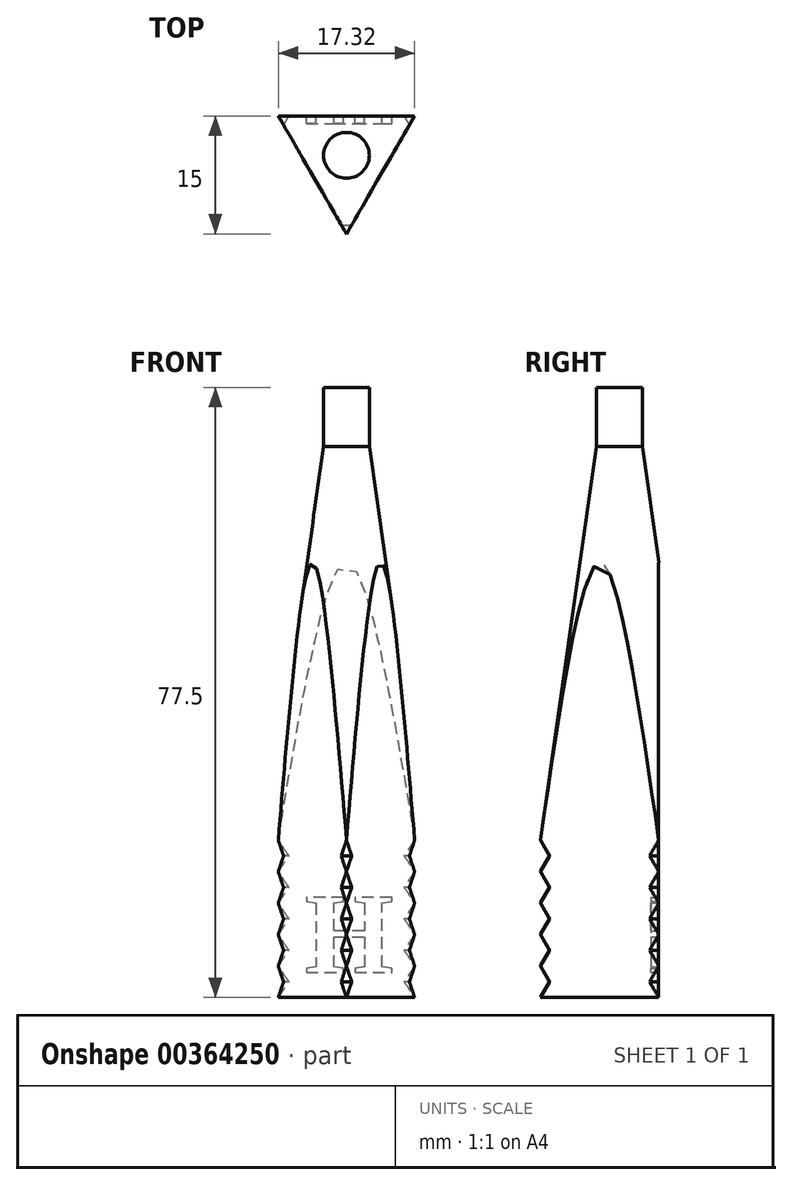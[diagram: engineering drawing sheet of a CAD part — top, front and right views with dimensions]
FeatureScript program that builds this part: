
annotation { "Feature Type Name" : "Feature", "Feature Type Description" : "" }
export const myFeature = defineFeature(function(context is Context, id is Id, definition is map)
    precondition{}
    {
        {
            var Q0;
            Q0=qCreatedBy(makeId("Top.planeOp"),FACE);
            var sketch = newSketch(context, id + "F0", { "sketchPlane" : qUnion([Q0])});
            skCircle(sketch, "E0", {"center": v(0, 0) * mm, "radius": 10 * mm, "construction": true});
            skLineSegment(sketch, "E1", {"start": v(0, -10) * mm, "end": v(-8.66, 5) * mm});
            skLineSegment(sketch, "E2", {"start": v(-8.66, 5) * mm, "end": v(8.66, 5) * mm});
            skLineSegment(sketch, "E3", {"start": v(8.66, 5) * mm, "end": v(0, -10) * mm});
            skSolve(sketch);
        }
        {
            var Q0;
            Q0=makeQuery(id+"F0.imprint","IMPRINT",FACE,{"disambiguationData":[TD([[makeQuery(id+"F0.imprint","IMPRINT",EDGE,{"derivedFrom":sQuery(id+"F0.wireOp",EDGE,"E1")}),-1.0]])]});
            extrude(context, id + "F1", {"entities" : qUnion([Q0]), "offsetDistance" : 25 * mm, "depth" : 20 * mm});
        }
        {
            var Q0;
            Q0=qCreatedBy(makeId("Right.planeOp"),FACE);
            var sketch = newSketch(context, id + "F2", { "sketchPlane" : qUnion([Q0])});
            skLineSegment(sketch, "E4", {"start": v(-2.91, 70) * mm, "end": v(-10, 20) * mm});
            skLineSegment(sketch, "E5", {"start": v(-10, 20) * mm, "end": v(0, 20) * mm});
            skLineSegment(sketch, "E6", {"start": v(0, 20) * mm, "end": v(0, 70) * mm});
            skLineSegment(sketch, "E7", {"start": v(-2.91, 70) * mm, "end": v(0, 70) * mm, "construction": true});
            skLineSegment(sketch, "E8", {"start": v(-2.91, 70) * mm, "end": v(-2.91, 76.5) * mm});
            skLineSegment(sketch, "E9", {"start": v(-2.91, 76.5) * mm, "end": v(0, 76.5) * mm});
            skLineSegment(sketch, "E10", {"start": v(0, 76.5) * mm, "end": v(0, 70) * mm});
            skSolve(sketch);
        }
        {
            var Q0;
            Q0=makeQuery(id+"F2.imprint","IMPRINT",FACE,{"disambiguationData":[TD([[makeQuery(id+"F2.imprint","IMPRINT",EDGE,{"derivedFrom":sQuery(id+"F2.wireOp",EDGE,"E4")}),1.0]])]});
            var Q1;
            Q1=sQuery(id+"F2.wireOp",EDGE,"E6");
            revolve(context, id + "F3", {"operationType" : NewBodyOperationType.ADD, "entities" : qUnion([Q0]), "axis" : qUnion([Q1]), "revolveType" : RevolveType.FULL});
        }
        {
            var Q0;
            Q0=qCreatedBy(makeId("Front.planeOp"),FACE);
            var sketch = newSketch(context, id + "F4", { "sketchPlane" : qUnion([Q0])});
            skLineSegment(sketch, "E11", {"start": v(-10, 20) * mm, "end": v(-10, 0) * mm});
            skLineSegment(sketch, "E12", {"start": v(-10, 20) * mm, "end": v(-8.86, 18) * mm});
            skLineSegment(sketch, "E13", {"start": v(-8.86, 18) * mm, "end": v(-10, 16) * mm});
            skLineSegment(sketch, "E14", {"start": v(-10, 20) * mm, "end": v(-10, 16) * mm, "construction": true});
            skLineSegment(sketch, "E15.0.1.0", {"start": v(-10, 16) * mm, "end": v(-8.86, 14) * mm});
            skLineSegment(sketch, "E15.0.1.1", {"start": v(-8.86, 14) * mm, "end": v(-10, 12) * mm});
            skLineSegment(sketch, "E15.0.2.0", {"start": v(-10, 12) * mm, "end": v(-8.86, 10) * mm});
            skLineSegment(sketch, "E15.0.2.1", {"start": v(-8.86, 10) * mm, "end": v(-10, 8) * mm});
            skLineSegment(sketch, "E15.0.3.0", {"start": v(-10, 8) * mm, "end": v(-8.86, 6) * mm});
            skLineSegment(sketch, "E15.0.3.1", {"start": v(-8.86, 6) * mm, "end": v(-10, 4) * mm});
            skLineSegment(sketch, "E15.0.4.0", {"start": v(-10, 4) * mm, "end": v(-8.86, 2) * mm});
            skLineSegment(sketch, "E15.0.4.1", {"start": v(-8.86, 2) * mm, "end": v(-10, 0) * mm});
            skLineSegment(sketch, "E15.direction1", {"start": v(-10, 20) * mm, "end": v(15, 20) * mm, "construction": true});
            skLineSegment(sketch, "E16", {"start": v(0, 11.1) * mm, "end": v(0, 0) * mm, "construction": true});
            skLineSegment(sketch, "E17", {"start": v(-8.86, 18) * mm, "end": v(-10, 18) * mm, "construction": true});
            skLineSegment(sketch, "E18", {"start": v(-8.86, 14) * mm, "end": v(-10, 14) * mm, "construction": true});
            skLineSegment(sketch, "E19", {"start": v(-8.86, 10) * mm, "end": v(-10, 10) * mm, "construction": true});
            skLineSegment(sketch, "E20", {"start": v(-8.86, 6) * mm, "end": v(-10, 6) * mm, "construction": true});
            skLineSegment(sketch, "E21", {"start": v(-8.86, 2) * mm, "end": v(-10, 2) * mm, "construction": true});
            skSolve(sketch);
        }
        {
            var Q0;
            Q0=qSketchRegion(id+"F4",true);
            var Q1;
            Q1=sQuery(id+"F4.wireOp",EDGE,"E16");
            revolve(context, id + "F5", {"operationType" : NewBodyOperationType.REMOVE, "entities" : qUnion([Q0]), "axis" : qUnion([Q1]), "revolveType" : RevolveType.FULL});
        }
        {
            var Q0;
            Q0=makeQuery(id+"F3.opRevolve","SWEPT_FACE",FACE,{"disambiguationData":[OSD([sQuery(id+"F2.wireOp",EDGE,"E9")])]});
            extrude(context, id + "F6", {"entities" : qUnion([Q0]), "operationType" : NewBodyOperationType.ADD, "depth" : 1 * mm});
        }
        {
            var Q0;
            Q0=makeQuery(id+"F3.boolean.opBoolean","SPLIT",FACE,{"disambiguationData":[OD(0.0)],"derivedFrom":makeQuery(id+"F3.opRevolve","SWEPT_FACE",FACE,{"disambiguationData":[OSD([sQuery(id+"F2.wireOp",EDGE,"E5")])]})});
            var Q1;
            Q1=makeQuery(id+"F3.boolean.opBoolean","SPLIT",FACE,{"disambiguationData":[OD(1.0)],"derivedFrom":makeQuery(id+"F3.opRevolve","SWEPT_FACE",FACE,{"disambiguationData":[OSD([sQuery(id+"F2.wireOp",EDGE,"E5")])]})});
            var Q2;
            Q2=makeQuery(id+"F3.boolean.opBoolean","SPLIT",FACE,{"disambiguationData":[OD(2.0)],"derivedFrom":makeQuery(id+"F3.opRevolve","SWEPT_FACE",FACE,{"disambiguationData":[OSD([sQuery(id+"F2.wireOp",EDGE,"E5")])]})});
            extrude(context, id + "F7", {"entities" : qUnion([Q0, Q1, Q2]), "operationType" : NewBodyOperationType.REMOVE, "oppositeDirection" : true, "depth" : 55.6 * mm, "offsetDistance" : 25 * mm});
        }
        {
            var Q0;
            {var subQ0=sQuery(id+"F0.wireOp",EDGE,"E2");Q0=makeQuery(id+"F7.boolean.opBoolean","MERGE",FACE,{"derivedFrom":[makeQuery(id+"F1.opExtrude","SWEPT_FACE",FACE,{"disambiguationData":[OSD([subQ0])]})],"fromTools":[makeQuery(id+"F7.opExtrude","SWEPT_FACE",FACE,{"disambiguationData":[OSD([subQ0])]})]});}
            var sketch = newSketch(context, id + "F8", { "sketchPlane" : qUnion([Q0])});
            skText(sketch, "E22", { "text": "H", "fontName": "Tinos-Bold.ttf"});
            const initialGuessF8  = {"E22": [-0.006, 0.00318, 1, 0, 0.01049]};
            skSetInitialGuess(sketch, initialGuessF8);
            skSolve(sketch);
        }
        {
            var Q0;
            Q0=makeQuery(id+"F8.imprint","IMPRINT",FACE,{"disambiguationData":[TD([[makeQuery(id+"F8.imprint","IMPRINT",EDGE,{"derivedFrom":sQuery(id+"F8.wireOp",EDGE,"E22.sketch_text.stroke-0")}),-1.0]])]});
            extrude(context, id + "F9", {"entities" : qUnion([Q0]), "operationType" : NewBodyOperationType.REMOVE, "oppositeDirection" : true, "depth" : 1 * mm, "offsetDistance" : 25 * mm});
        }
        {
            var Q0;
            Q0=qCreatedBy(makeId("Right.planeOp"),FACE);
            var sketch = newSketch(context, id + "F10", { "sketchPlane" : qUnion([Q0])});
            skLineSegment(sketch, "E23", {"start": v(0, -1.77) * mm, "end": v(0, -40.68) * mm, "construction": true});
            skSolve(sketch);
        }
    });
